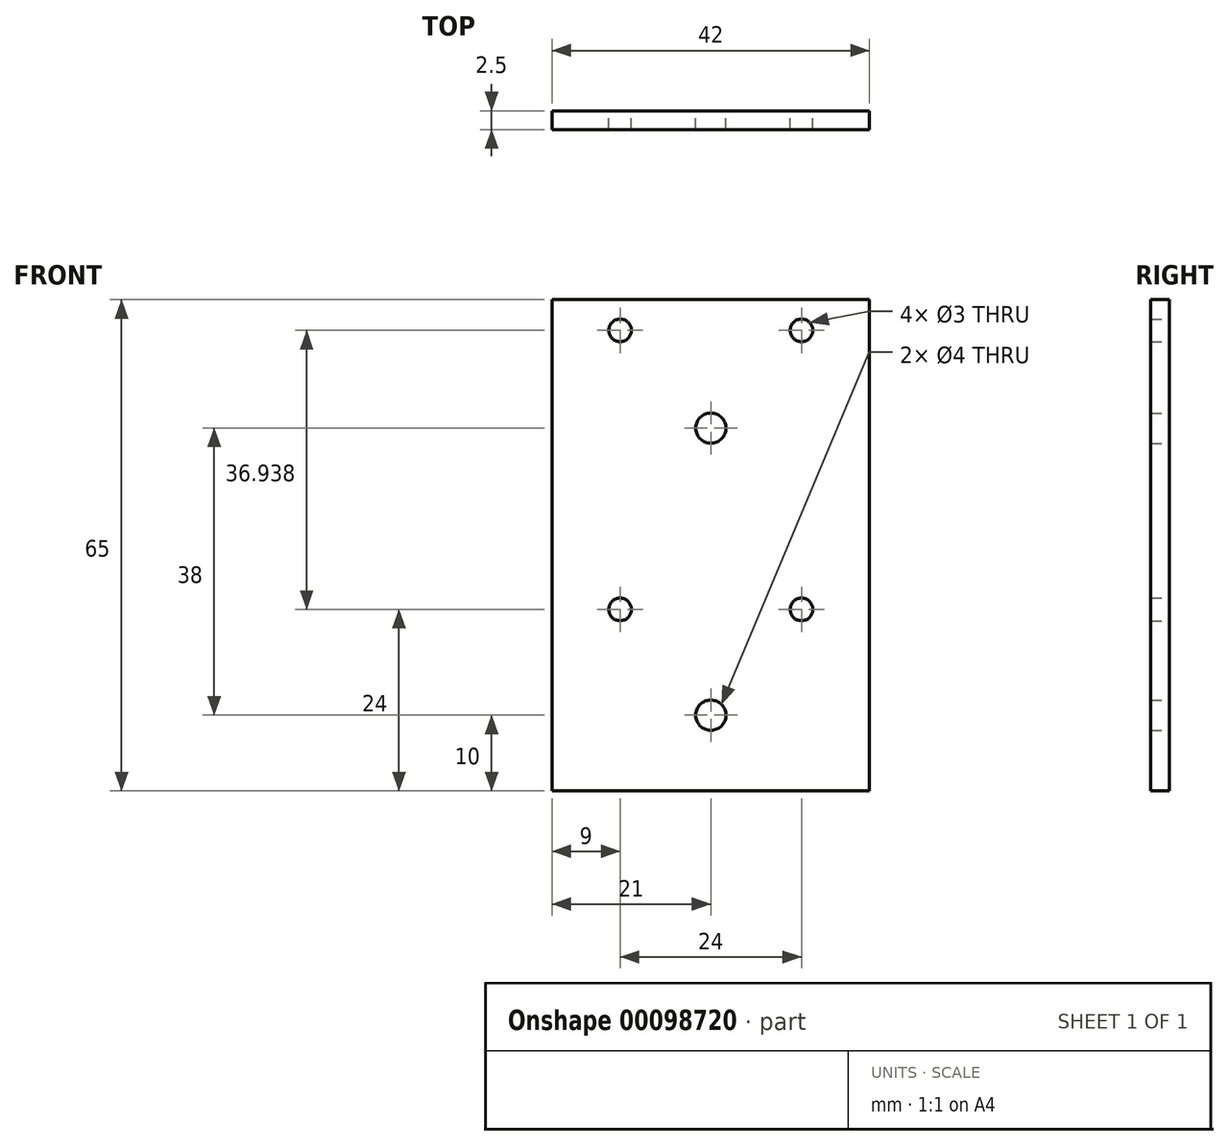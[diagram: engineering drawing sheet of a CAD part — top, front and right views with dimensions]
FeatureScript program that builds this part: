
annotation { "Feature Type Name" : "Feature", "Feature Type Description" : "" }
export const myFeature = defineFeature(function(context is Context, id is Id, definition is map)
    precondition{}
    {
        {
            var Q0;
            Q0=qCreatedBy(makeId("Front.planeOp"),FACE);
            var sketch = newSketch(context, id + "F0", { "sketchPlane" : qUnion([Q0])});
            skCircle(sketch, "E0", {"center": v(0, -22.5) * mm, "radius": 2 * mm});
            skCircle(sketch, "E1", {"center": v(0, 15.5) * mm, "radius": 2 * mm});
            skLineSegment(sketch, "E2", {"start": v(-21, -32.5) * mm, "end": v(-21, 32.5) * mm});
            skLineSegment(sketch, "E3", {"start": v(-21, 32.5) * mm, "end": v(21, 32.5) * mm});
            skLineSegment(sketch, "E4", {"start": v(21, 32.5) * mm, "end": v(21, -32.5) * mm});
            skLineSegment(sketch, "E5", {"start": v(21, -32.5) * mm, "end": v(-21, -32.5) * mm});
            skCircle(sketch, "E6", {"center": v(-12, 28.44) * mm, "radius": 1.5 * mm});
            skCircle(sketch, "E7", {"center": v(12, 28.44) * mm, "radius": 1.5 * mm});
            skCircle(sketch, "E8", {"center": v(-12, -8.5) * mm, "radius": 1.5 * mm});
            skCircle(sketch, "E9", {"center": v(12, -8.5) * mm, "radius": 1.5 * mm});
            skSolve(sketch);
        }
        {
            var Q0;
            Q0 = qSketchRegion(id + "F0", true);
            extrude(context, id + "F1", {"entities" : qUnion([Q0]), "depth" : 2.5 * mm, "symmetric" : true});
        }
    });
